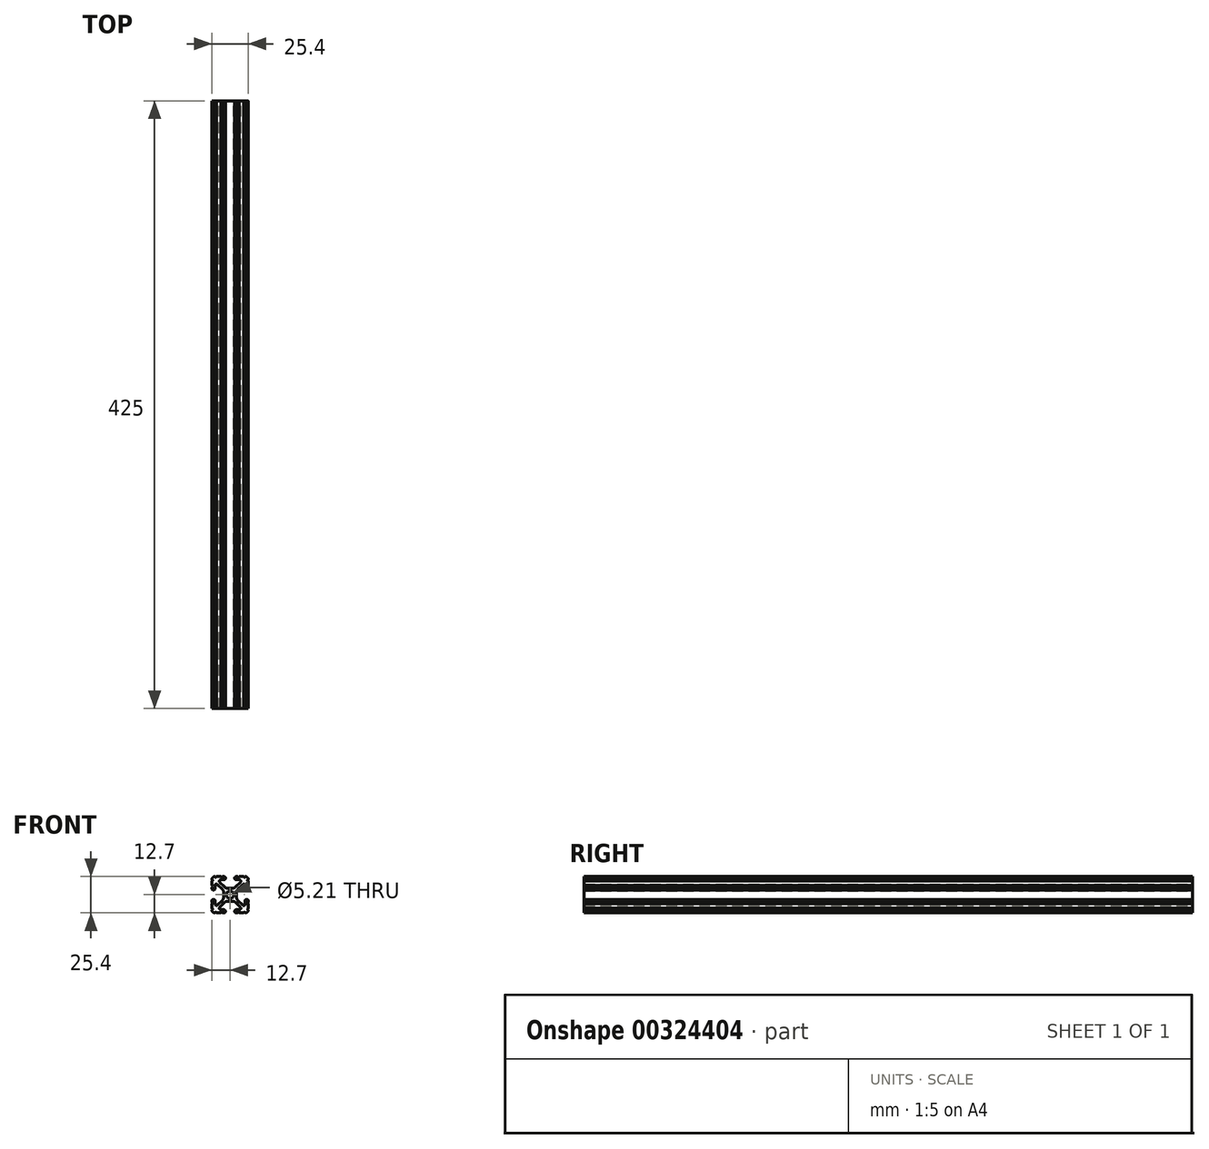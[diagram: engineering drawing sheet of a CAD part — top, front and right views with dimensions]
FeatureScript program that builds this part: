
annotation { "Feature Type Name" : "Feature", "Feature Type Description" : "" }
export const myFeature = defineFeature(function(context is Context, id is Id, definition is map)
    precondition{}
    {
        {
            var Q0;
            Q0=qCreatedBy(makeId("Front.planeOp"),FACE);
            var sketch = newSketch(context, id + "F0", { "sketchPlane" : qUnion([Q0])});
            skArc(sketch, "E0", {"start": v(-12.7, -10.57) * mm, "mid": v(-12.2, -10.06) * mm, "end": v(-12.7, -9.55) * mm});
            skArc(sketch, "E1", {"start": v(-12.7, -10.57) * mm, "mid": v(-12.08, -12.08) * mm, "end": v(-10.57, -12.7) * mm});
            skArc(sketch, "E2", {"start": v(-9.55, -12.7) * mm, "mid": v(-10.06, -12.2) * mm, "end": v(-10.57, -12.7) * mm});
            skLineSegment(sketch, "E3", {"start": v(-9.55, -12.7) * mm, "end": v(-6.33, -12.7) * mm});
            skArc(sketch, "E4", {"start": v(-5.32, -12.7) * mm, "mid": v(-5.83, -12.2) * mm, "end": v(-6.33, -12.7) * mm});
            skLineSegment(sketch, "E5", {"start": v(-5.32, -12.7) * mm, "end": v(-4.34, -12.7) * mm});
            skArc(sketch, "E6", {"start": v(-4.34, -12.7) * mm, "mid": v(-3.24, -11.6) * mm, "end": v(-4.34, -10.5) * mm});
            skLineSegment(sketch, "E7", {"start": v(-4.34, -10.5) * mm, "end": v(-6.47, -10.5) * mm});
            skArc(sketch, "E8", {"start": v(-7.2, -8.76) * mm, "mid": v(-7.41, -9.86) * mm, "end": v(-6.47, -10.5) * mm});
            skLineSegment(sketch, "E9", {"start": v(-7.2, -8.76) * mm, "end": v(-3.86, -5.43) * mm});
            skArc(sketch, "E10", {"start": v(-1.62, -4.5) * mm, "mid": v(-2.83, -4.74) * mm, "end": v(-3.86, -5.43) * mm});
            skLineSegment(sketch, "E11", {"start": v(-1.62, -4.5) * mm, "end": v(1.62, -4.5) * mm});
            skArc(sketch, "E12", {"start": v(3.86, -5.43) * mm, "mid": v(2.83, -4.74) * mm, "end": v(1.62, -4.5) * mm});
            skLineSegment(sketch, "E13", {"start": v(3.86, -5.43) * mm, "end": v(7.2, -8.76) * mm});
            skArc(sketch, "E14", {"start": v(6.47, -10.5) * mm, "mid": v(7.41, -9.86) * mm, "end": v(7.2, -8.76) * mm});
            skLineSegment(sketch, "E15", {"start": v(6.47, -10.5) * mm, "end": v(4.34, -10.5) * mm});
            skArc(sketch, "E16", {"start": v(4.34, -10.5) * mm, "mid": v(3.24, -11.6) * mm, "end": v(4.34, -12.7) * mm});
            skLineSegment(sketch, "E17", {"start": v(4.34, -12.7) * mm, "end": v(5.32, -12.7) * mm});
            skArc(sketch, "E18", {"start": v(6.33, -12.7) * mm, "mid": v(5.83, -12.2) * mm, "end": v(5.32, -12.7) * mm});
            skLineSegment(sketch, "E19", {"start": v(6.33, -12.7) * mm, "end": v(9.55, -12.7) * mm});
            skArc(sketch, "E20", {"start": v(10.57, -12.7) * mm, "mid": v(10.06, -12.2) * mm, "end": v(9.55, -12.7) * mm});
            skArc(sketch, "E21", {"start": v(10.57, -12.7) * mm, "mid": v(12.08, -12.08) * mm, "end": v(12.7, -10.57) * mm});
            skArc(sketch, "E22", {"start": v(12.7, -9.55) * mm, "mid": v(12.2, -10.06) * mm, "end": v(12.7, -10.57) * mm});
            skLineSegment(sketch, "E23", {"start": v(12.7, -9.55) * mm, "end": v(12.7, -6.33) * mm});
            skArc(sketch, "E24", {"start": v(12.7, -5.32) * mm, "mid": v(12.2, -5.83) * mm, "end": v(12.7, -6.33) * mm});
            skLineSegment(sketch, "E25", {"start": v(12.7, -5.32) * mm, "end": v(12.7, -4.34) * mm});
            skArc(sketch, "E26", {"start": v(12.7, -4.34) * mm, "mid": v(11.6, -3.24) * mm, "end": v(10.5, -4.34) * mm});
            skLineSegment(sketch, "E27", {"start": v(10.5, -4.34) * mm, "end": v(10.5, -6.47) * mm});
            skArc(sketch, "E28", {"start": v(8.76, -7.2) * mm, "mid": v(9.86, -7.41) * mm, "end": v(10.5, -6.47) * mm});
            skLineSegment(sketch, "E29", {"start": v(8.76, -7.2) * mm, "end": v(5.43, -3.86) * mm});
            skArc(sketch, "E30", {"start": v(4.5, -1.62) * mm, "mid": v(4.74, -2.83) * mm, "end": v(5.43, -3.86) * mm});
            skLineSegment(sketch, "E31", {"start": v(4.5, -1.62) * mm, "end": v(4.5, 1.62) * mm});
            skArc(sketch, "E32", {"start": v(5.43, 3.86) * mm, "mid": v(4.74, 2.83) * mm, "end": v(4.5, 1.62) * mm});
            skLineSegment(sketch, "E33", {"start": v(5.43, 3.86) * mm, "end": v(8.76, 7.2) * mm});
            skArc(sketch, "E34", {"start": v(10.5, 6.47) * mm, "mid": v(9.86, 7.41) * mm, "end": v(8.76, 7.2) * mm});
            skLineSegment(sketch, "E35", {"start": v(10.5, 6.47) * mm, "end": v(10.5, 4.34) * mm});
            skArc(sketch, "E36", {"start": v(10.5, 4.34) * mm, "mid": v(11.6, 3.24) * mm, "end": v(12.7, 4.34) * mm});
            skLineSegment(sketch, "E37", {"start": v(12.7, 4.34) * mm, "end": v(12.7, 5.32) * mm});
            skArc(sketch, "E38", {"start": v(12.7, 6.33) * mm, "mid": v(12.2, 5.83) * mm, "end": v(12.7, 5.32) * mm});
            skLineSegment(sketch, "E39", {"start": v(12.7, 6.33) * mm, "end": v(12.7, 9.55) * mm});
            skArc(sketch, "E40", {"start": v(12.7, 10.57) * mm, "mid": v(12.2, 10.06) * mm, "end": v(12.7, 9.55) * mm});
            skArc(sketch, "E41", {"start": v(12.7, 10.57) * mm, "mid": v(12.08, 12.08) * mm, "end": v(10.57, 12.7) * mm});
            skArc(sketch, "E42", {"start": v(9.55, 12.7) * mm, "mid": v(10.06, 12.2) * mm, "end": v(10.57, 12.7) * mm});
            skLineSegment(sketch, "E43", {"start": v(9.55, 12.7) * mm, "end": v(6.33, 12.7) * mm});
            skArc(sketch, "E44", {"start": v(5.32, 12.7) * mm, "mid": v(5.83, 12.2) * mm, "end": v(6.33, 12.7) * mm});
            skLineSegment(sketch, "E45", {"start": v(5.32, 12.7) * mm, "end": v(4.34, 12.7) * mm});
            skArc(sketch, "E46", {"start": v(4.34, 12.7) * mm, "mid": v(3.24, 11.6) * mm, "end": v(4.34, 10.5) * mm});
            skLineSegment(sketch, "E47", {"start": v(4.34, 10.5) * mm, "end": v(6.47, 10.5) * mm});
            skArc(sketch, "E48", {"start": v(7.2, 8.76) * mm, "mid": v(7.41, 9.86) * mm, "end": v(6.47, 10.5) * mm});
            skLineSegment(sketch, "E49", {"start": v(7.2, 8.76) * mm, "end": v(3.86, 5.43) * mm});
            skArc(sketch, "E50", {"start": v(1.62, 4.5) * mm, "mid": v(2.83, 4.74) * mm, "end": v(3.86, 5.43) * mm});
            skLineSegment(sketch, "E51", {"start": v(1.62, 4.5) * mm, "end": v(-1.62, 4.5) * mm});
            skArc(sketch, "E52", {"start": v(-3.86, 5.43) * mm, "mid": v(-2.83, 4.74) * mm, "end": v(-1.62, 4.5) * mm});
            skLineSegment(sketch, "E53", {"start": v(-3.86, 5.43) * mm, "end": v(-7.2, 8.76) * mm});
            skArc(sketch, "E54", {"start": v(-6.47, 10.5) * mm, "mid": v(-7.41, 9.86) * mm, "end": v(-7.2, 8.76) * mm});
            skLineSegment(sketch, "E55", {"start": v(-6.47, 10.5) * mm, "end": v(-4.34, 10.5) * mm});
            skArc(sketch, "E56", {"start": v(-4.34, 10.5) * mm, "mid": v(-3.24, 11.6) * mm, "end": v(-4.34, 12.7) * mm});
            skLineSegment(sketch, "E57", {"start": v(-4.34, 12.7) * mm, "end": v(-5.32, 12.7) * mm});
            skArc(sketch, "E58", {"start": v(-6.33, 12.7) * mm, "mid": v(-5.83, 12.2) * mm, "end": v(-5.32, 12.7) * mm});
            skLineSegment(sketch, "E59", {"start": v(-6.33, 12.7) * mm, "end": v(-9.55, 12.7) * mm});
            skArc(sketch, "E60", {"start": v(-10.57, 12.7) * mm, "mid": v(-10.06, 12.2) * mm, "end": v(-9.55, 12.7) * mm});
            skArc(sketch, "E61", {"start": v(-10.57, 12.7) * mm, "mid": v(-12.08, 12.08) * mm, "end": v(-12.7, 10.57) * mm});
            skArc(sketch, "E62", {"start": v(-12.7, 9.55) * mm, "mid": v(-12.2, 10.06) * mm, "end": v(-12.7, 10.57) * mm});
            skLineSegment(sketch, "E63", {"start": v(-12.7, 9.55) * mm, "end": v(-12.7, 6.33) * mm});
            skArc(sketch, "E64", {"start": v(-12.7, 5.32) * mm, "mid": v(-12.2, 5.83) * mm, "end": v(-12.7, 6.33) * mm});
            skLineSegment(sketch, "E65", {"start": v(-12.7, 5.32) * mm, "end": v(-12.7, 4.34) * mm});
            skArc(sketch, "E66", {"start": v(-12.7, 4.34) * mm, "mid": v(-11.6, 3.24) * mm, "end": v(-10.5, 4.34) * mm});
            skLineSegment(sketch, "E67", {"start": v(-10.5, 4.34) * mm, "end": v(-10.5, 6.47) * mm});
            skArc(sketch, "E68", {"start": v(-8.76, 7.2) * mm, "mid": v(-9.86, 7.41) * mm, "end": v(-10.5, 6.47) * mm});
            skLineSegment(sketch, "E69", {"start": v(-8.76, 7.2) * mm, "end": v(-5.43, 3.86) * mm});
            skArc(sketch, "E70", {"start": v(-4.5, 1.62) * mm, "mid": v(-4.74, 2.83) * mm, "end": v(-5.43, 3.86) * mm});
            skLineSegment(sketch, "E71", {"start": v(-4.5, 1.62) * mm, "end": v(-4.5, -1.62) * mm});
            skArc(sketch, "E72", {"start": v(-5.43, -3.86) * mm, "mid": v(-4.74, -2.83) * mm, "end": v(-4.5, -1.62) * mm});
            skLineSegment(sketch, "E73", {"start": v(-5.43, -3.86) * mm, "end": v(-8.76, -7.2) * mm});
            skArc(sketch, "E74", {"start": v(-10.5, -6.47) * mm, "mid": v(-9.86, -7.41) * mm, "end": v(-8.76, -7.2) * mm});
            skLineSegment(sketch, "E75", {"start": v(-10.5, -6.47) * mm, "end": v(-10.5, -4.34) * mm});
            skArc(sketch, "E76", {"start": v(-10.5, -4.34) * mm, "mid": v(-11.6, -3.24) * mm, "end": v(-12.7, -4.34) * mm});
            skLineSegment(sketch, "E77", {"start": v(-12.7, -4.34) * mm, "end": v(-12.7, -5.32) * mm});
            skArc(sketch, "E78", {"start": v(-12.7, -6.33) * mm, "mid": v(-12.2, -5.83) * mm, "end": v(-12.7, -5.32) * mm});
            skLineSegment(sketch, "E79", {"start": v(-12.7, -6.33) * mm, "end": v(-12.7, -9.55) * mm});
            skArc(sketch, "E80", {"start": v(2.6, 0) * mm, "mid": v(0, 2.6) * mm, "end": v(-2.6, 0) * mm});
            skArc(sketch, "E81", {"start": v(-2.6, 0) * mm, "mid": v(0, -2.6) * mm, "end": v(2.6, 0) * mm});
            skSolve(sketch);
        }
        {
            var Q0;
            Q0=makeQuery(id+"F0.imprint","IMPRINT",FACE,{"disambiguationData":[TD([[makeQuery(id+"F0.imprint","IMPRINT",EDGE,{"derivedFrom":sQuery(id+"F0.wireOp",EDGE,"E0")}),-1.0]])]});
            extrude(context, id + "F1", {"entities" : qUnion([Q0]), "depth" : 425 * mm});
        }
        {
            var Q0;
            Q0=makeQuery(id+"F1.opExtrude","CAP_FACE",FACE,{"disambiguationData":[OSD([sQuery(id+"F0.wireOp",EDGE,"E0"),sQuery(id+"F0.wireOp",EDGE,"E1"),sQuery(id+"F0.wireOp",EDGE,"E2"),sQuery(id+"F0.wireOp",EDGE,"E3"),sQuery(id+"F0.wireOp",EDGE,"E4"),sQuery(id+"F0.wireOp",EDGE,"E5"),sQuery(id+"F0.wireOp",EDGE,"E6"),sQuery(id+"F0.wireOp",EDGE,"E7"),sQuery(id+"F0.wireOp",EDGE,"E8"),sQuery(id+"F0.wireOp",EDGE,"E9"),sQuery(id+"F0.wireOp",EDGE,"E10"),sQuery(id+"F0.wireOp",EDGE,"E11"),sQuery(id+"F0.wireOp",EDGE,"E12"),sQuery(id+"F0.wireOp",EDGE,"E13"),sQuery(id+"F0.wireOp",EDGE,"E14"),sQuery(id+"F0.wireOp",EDGE,"E15"),sQuery(id+"F0.wireOp",EDGE,"E16"),sQuery(id+"F0.wireOp",EDGE,"E17"),sQuery(id+"F0.wireOp",EDGE,"E18"),sQuery(id+"F0.wireOp",EDGE,"E19"),sQuery(id+"F0.wireOp",EDGE,"E20"),sQuery(id+"F0.wireOp",EDGE,"E21"),sQuery(id+"F0.wireOp",EDGE,"E22"),sQuery(id+"F0.wireOp",EDGE,"E23"),sQuery(id+"F0.wireOp",EDGE,"E24"),sQuery(id+"F0.wireOp",EDGE,"E25"),sQuery(id+"F0.wireOp",EDGE,"E26"),sQuery(id+"F0.wireOp",EDGE,"E27"),sQuery(id+"F0.wireOp",EDGE,"E28"),sQuery(id+"F0.wireOp",EDGE,"E29"),sQuery(id+"F0.wireOp",EDGE,"E30"),sQuery(id+"F0.wireOp",EDGE,"E31"),sQuery(id+"F0.wireOp",EDGE,"E32"),sQuery(id+"F0.wireOp",EDGE,"E33"),sQuery(id+"F0.wireOp",EDGE,"E34"),sQuery(id+"F0.wireOp",EDGE,"E35"),sQuery(id+"F0.wireOp",EDGE,"E36"),sQuery(id+"F0.wireOp",EDGE,"E37"),sQuery(id+"F0.wireOp",EDGE,"E38"),sQuery(id+"F0.wireOp",EDGE,"E39"),sQuery(id+"F0.wireOp",EDGE,"E40"),sQuery(id+"F0.wireOp",EDGE,"E41"),sQuery(id+"F0.wireOp",EDGE,"E42"),sQuery(id+"F0.wireOp",EDGE,"E43"),sQuery(id+"F0.wireOp",EDGE,"E44"),sQuery(id+"F0.wireOp",EDGE,"E45"),sQuery(id+"F0.wireOp",EDGE,"E46"),sQuery(id+"F0.wireOp",EDGE,"E47"),sQuery(id+"F0.wireOp",EDGE,"E48"),sQuery(id+"F0.wireOp",EDGE,"E49"),sQuery(id+"F0.wireOp",EDGE,"E50"),sQuery(id+"F0.wireOp",EDGE,"E51"),sQuery(id+"F0.wireOp",EDGE,"E52"),sQuery(id+"F0.wireOp",EDGE,"E53"),sQuery(id+"F0.wireOp",EDGE,"E54"),sQuery(id+"F0.wireOp",EDGE,"E55"),sQuery(id+"F0.wireOp",EDGE,"E56"),sQuery(id+"F0.wireOp",EDGE,"E57"),sQuery(id+"F0.wireOp",EDGE,"E58"),sQuery(id+"F0.wireOp",EDGE,"E59"),sQuery(id+"F0.wireOp",EDGE,"E60"),sQuery(id+"F0.wireOp",EDGE,"E61"),sQuery(id+"F0.wireOp",EDGE,"E62"),sQuery(id+"F0.wireOp",EDGE,"E63"),sQuery(id+"F0.wireOp",EDGE,"E64"),sQuery(id+"F0.wireOp",EDGE,"E65"),sQuery(id+"F0.wireOp",EDGE,"E66"),sQuery(id+"F0.wireOp",EDGE,"E67"),sQuery(id+"F0.wireOp",EDGE,"E68"),sQuery(id+"F0.wireOp",EDGE,"E69"),sQuery(id+"F0.wireOp",EDGE,"E70"),sQuery(id+"F0.wireOp",EDGE,"E71"),sQuery(id+"F0.wireOp",EDGE,"E72"),sQuery(id+"F0.wireOp",EDGE,"E73"),sQuery(id+"F0.wireOp",EDGE,"E74"),sQuery(id+"F0.wireOp",EDGE,"E75"),sQuery(id+"F0.wireOp",EDGE,"E76"),sQuery(id+"F0.wireOp",EDGE,"E77"),sQuery(id+"F0.wireOp",EDGE,"E78"),sQuery(id+"F0.wireOp",EDGE,"E79"),sQuery(id+"F0.wireOp",EDGE,"E80"),sQuery(id+"F0.wireOp",EDGE,"E81")])],"isStart":false});
            var sketch = newSketch(context, id + "F2", { "sketchPlane" : qUnion([Q0])});
            skLineSegment(sketch, "E82", {"start": v(-4.34, 12.7) * mm, "end": v(5.32, 12.7) * mm, "construction": true});
            skPoint(sketch, "E83", {"position": v(0.49, 12.7) * mm});
            skSolve(sketch);
        }
    });
